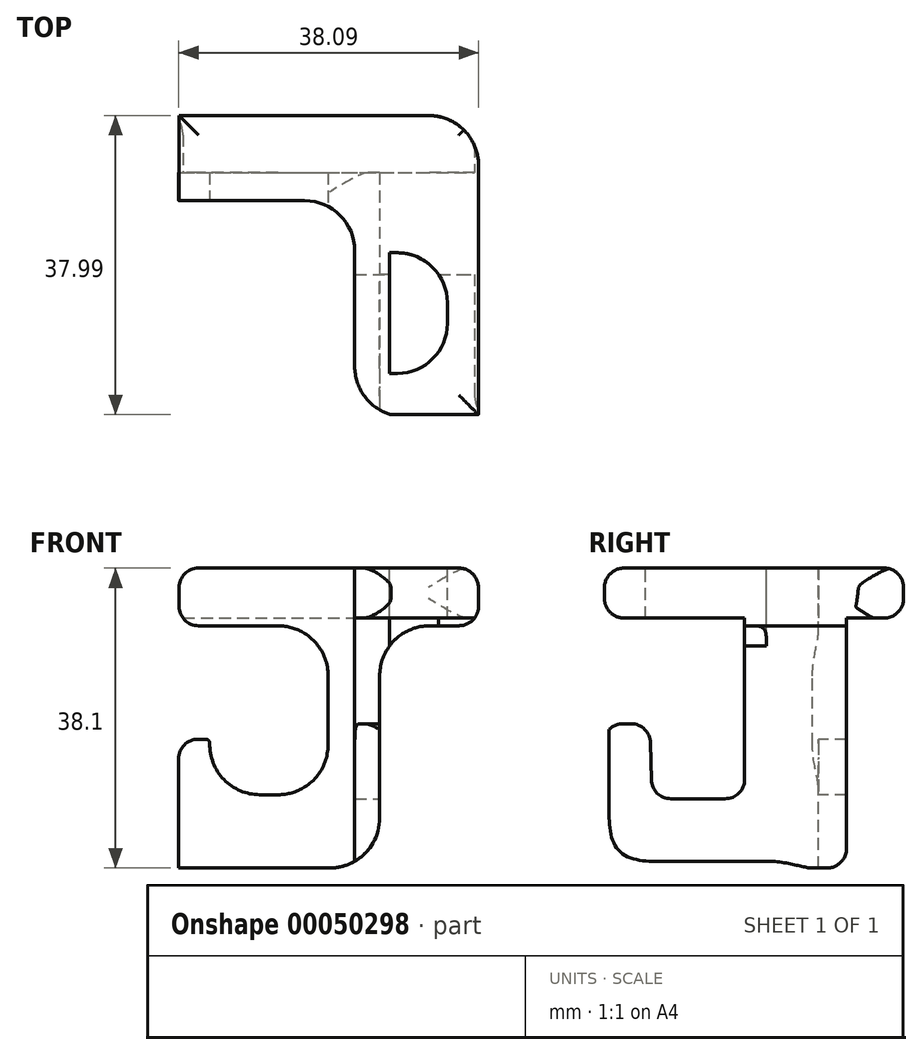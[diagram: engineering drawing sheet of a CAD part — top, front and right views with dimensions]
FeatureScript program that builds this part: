
annotation { "Feature Type Name" : "Feature", "Feature Type Description" : "" }
export const myFeature = defineFeature(function(context is Context, id is Id, definition is map)
    precondition{}
    {
        {
            var Q0;
            Q0=qCreatedBy(makeId("Front.planeOp"),FACE);
            var sketch = newSketch(context, id + "F0", { "sketchPlane" : qUnion([Q0])});
            skLineSegment(sketch, "E0", {"start": v(0, 0) * mm, "end": v(38.1, 0) * mm});
            skLineSegment(sketch, "E1", {"start": v(38.1, 0) * mm, "end": v(38.1, 38.1) * mm});
            skLineSegment(sketch, "E2", {"start": v(38.1, 38.1) * mm, "end": v(0, 38.1) * mm});
            skLineSegment(sketch, "E3", {"start": v(0, 38.1) * mm, "end": v(0, 0) * mm});
            skSolve(sketch);
        }
        {
            var Q0;
            Q0 = qSketchRegion(id + "F0", true);
            extrude(context, id + "F1", {"entities" : qUnion([Q0]), "depth" : 38.1 * mm});
        }
        {
            var Q0;
            Q0=qCreatedBy(makeId("Top.planeOp"),FACE);
            cPlane(context, id + "F2", {"entities" : qUnion([Q0]), "cplaneType" : CPlaneType.OFFSET, "offset" : 38.1 * mm, "width" : 152.4 * mm, "height" : 152.4 * mm});
        }
        {
            var Q0;
            Q0=qCreatedBy(makeId("Front.planeOp"),FACE);
            cPlane(context, id + "F3", {"entities" : qUnion([Q0]), "cplaneType" : CPlaneType.OFFSET, "offset" : 38.1 * mm, "width" : 152.4 * mm, "height" : 152.4 * mm});
        }
        {
            var Q0;
            Q0=qCreatedBy(makeId("Right.planeOp"),FACE);
            cPlane(context, id + "F4", {"entities" : qUnion([Q0]), "cplaneType" : CPlaneType.OFFSET, "offset" : 38.1 * mm, "width" : 152.4 * mm, "height" : 152.4 * mm});
        }
        {
            var Q0;
            Q0=qCreatedBy(id+"F3.planeOp",FACE);
            var sketch = newSketch(context, id + "F5", { "sketchPlane" : qUnion([Q0])});
            skLineSegment(sketch, "E4.bottom", {"start": v(0, 0) * mm, "end": v(38.1, 0) * mm});
            skLineSegment(sketch, "E4.top", {"start": v(0, 38.1) * mm, "end": v(38.1, 38.1) * mm});
            skLineSegment(sketch, "E4.left", {"start": v(0, 0) * mm, "end": v(0, 38.1) * mm});
            skLineSegment(sketch, "E4.right", {"start": v(38.1, 0) * mm, "end": v(38.1, 38.1) * mm});
            skPoint(sketch, "E5.startSnap0", {"position": v(19.05, 38.1) * mm});
            skLineSegment(sketch, "E6", {"start": v(2.51, 30.77) * mm, "end": v(12.05, 30.77) * mm});
            skLineSegment(sketch, "E7", {"start": v(12.05, 30.77) * mm, "end": v(12.63, 30.77) * mm});
            skLineSegment(sketch, "E8", {"start": v(18.98, 24.42) * mm, "end": v(18.98, 15.66) * mm});
            skLineSegment(sketch, "E9", {"start": v(12.63, 9.3) * mm, "end": v(11.17, 9.3) * mm});
            skLineSegment(sketch, "E10", {"start": v(4, 0) * mm, "end": v(19.18, 0) * mm});
            skLineSegment(sketch, "E11", {"start": v(25.53, 6.35) * mm, "end": v(25.53, 24.42) * mm});
            skLineSegment(sketch, "E12", {"start": v(31.88, 30.77) * mm, "end": v(35.62, 30.77) * mm});
            skLineSegment(sketch, "E13.left", {"start": v(0, 38.1) * mm, "end": v(0, 0) * mm});
            skLineSegment(sketch, "E13.right", {"start": v(38.1, 38.1) * mm, "end": v(38.1, 0) * mm});
            skLineSegment(sketch, "E14", {"start": v(3.45, 16.36) * mm, "end": v(2.47, 16.36) * mm});
            skLineSegment(sketch, "E15", {"start": v(0, 13.89) * mm, "end": v(0, 0) * mm});
            skLineSegment(sketch, "E16", {"start": v(11.17, 9.3) * mm, "end": v(10.3, 9.3) * mm});
            skPoint(sketch, "E17.visualSharp", {"position": v(4, 9.3) * mm});
            skArc(sketch, "E17.filletArc", {"start": v(3.96, 15.84) * mm, "mid": v(5.75, 11.23) * mm, "end": v(10.3, 9.3) * mm});
            skPoint(sketch, "E18.visualSharp", {"position": v(18.98, 9.3) * mm});
            skArc(sketch, "E18.filletArc", {"start": v(12.63, 9.3) * mm, "mid": v(17.12, 11.17) * mm, "end": v(18.98, 15.66) * mm});
            skPoint(sketch, "E19.visualSharp", {"position": v(25.53, 0) * mm});
            skArc(sketch, "E19.filletArc", {"start": v(19.18, 0) * mm, "mid": v(23.67, 1.86) * mm, "end": v(25.53, 6.35) * mm});
            skPoint(sketch, "E20.visualSharp", {"position": v(18.98, 30.77) * mm});
            skArc(sketch, "E20.filletArc", {"start": v(18.98, 24.42) * mm, "mid": v(17.12, 28.91) * mm, "end": v(12.63, 30.77) * mm});
            skPoint(sketch, "E21.visualSharp", {"position": v(25.53, 30.77) * mm});
            skArc(sketch, "E21.filletArc", {"start": v(31.88, 30.77) * mm, "mid": v(27.4, 28.91) * mm, "end": v(25.53, 24.42) * mm});
            skPoint(sketch, "E22.visualSharp", {"position": v(0, 16.36) * mm});
            skArc(sketch, "E22.filletArc", {"start": v(2.47, 16.36) * mm, "mid": v(0.72, 15.63) * mm, "end": v(0, 13.89) * mm});
            skLineSegment(sketch, "E23", {"start": v(0.04, 33.24) * mm, "end": v(0.04, 35.63) * mm});
            skLineSegment(sketch, "E24", {"start": v(2.51, 38.1) * mm, "end": v(35.6, 38.1) * mm});
            skLineSegment(sketch, "E25", {"start": v(38.07, 35.65) * mm, "end": v(38.1, 33.27) * mm});
            skPoint(sketch, "E26.visualSharp", {"position": v(0.04, 30.77) * mm});
            skArc(sketch, "E26.filletArc", {"start": v(0.04, 33.24) * mm, "mid": v(0.77, 31.5) * mm, "end": v(2.51, 30.77) * mm});
            skPoint(sketch, "E27.visualSharp", {"position": v(38.12, 30.77) * mm});
            skArc(sketch, "E27.filletArc", {"start": v(35.62, 30.77) * mm, "mid": v(37.38, 31.5) * mm, "end": v(38.1, 33.27) * mm});
            skPoint(sketch, "E28.visualSharp", {"position": v(38.04, 38.1) * mm});
            skArc(sketch, "E28.filletArc", {"start": v(38.07, 35.65) * mm, "mid": v(37.34, 37.39) * mm, "end": v(35.6, 38.1) * mm});
            skPoint(sketch, "E29.visualSharp", {"position": v(0.04, 38.1) * mm});
            skArc(sketch, "E29.filletArc", {"start": v(2.51, 38.1) * mm, "mid": v(0.77, 37.38) * mm, "end": v(0.04, 35.63) * mm});
            skPoint(sketch, "E30.visualSharp", {"position": v(4, 16.36) * mm});
            skArc(sketch, "E30.filletArc", {"start": v(3.96, 15.84) * mm, "mid": v(3.81, 16.2) * mm, "end": v(3.45, 16.36) * mm});
            skSolve(sketch);
        }
        {
            var Q0;
            Q0=qCreatedBy(id+"F4.planeOp",FACE);
            var sketch = newSketch(context, id + "F6", { "sketchPlane" : qUnion([Q0])});
            skLineSegment(sketch, "E31", {"start": v(-29.2, 31.75) * mm, "end": v(-20.19, 31.75) * mm});
            skLineSegment(sketch, "E32", {"start": v(-34.61, 18.32) * mm, "end": v(-35.63, 18.32) * mm});
            skLineSegment(sketch, "E33", {"start": v(-38.1, 15.85) * mm, "end": v(-38.1, 2.47) * mm});
            skLineSegment(sketch, "E34", {"start": v(-35.63, 0) * mm, "end": v(-9.72, 0) * mm});
            skLineSegment(sketch, "E35", {"start": v(-7.25, 2.47) * mm, "end": v(-7.25, 31.75) * mm});
            skLineSegment(sketch, "E36", {"start": v(-7.25, 31.75) * mm, "end": v(-2.47, 31.75) * mm});
            skLineSegment(sketch, "E37", {"start": v(0, 34.22) * mm, "end": v(0, 35.63) * mm});
            skLineSegment(sketch, "E38", {"start": v(-2.47, 38.1) * mm, "end": v(-35.52, 38.1) * mm});
            skLineSegment(sketch, "E39", {"start": v(-38, 35.63) * mm, "end": v(-38, 34.22) * mm});
            skLineSegment(sketch, "E40", {"start": v(-35.52, 31.75) * mm, "end": v(-29.2, 31.75) * mm});
            skLineSegment(sketch, "E41", {"start": v(-20.19, 31.75) * mm, "end": v(-20.19, 11.27) * mm});
            skLineSegment(sketch, "E42", {"start": v(-22.66, 8.8) * mm, "end": v(-29.57, 8.8) * mm});
            skLineSegment(sketch, "E43", {"start": v(-32.04, 11.21) * mm, "end": v(-32.14, 15.9) * mm});
            skPoint(sketch, "E44.visualSharp", {"position": v(-38, 31.75) * mm});
            skArc(sketch, "E44.filletArc", {"start": v(-38, 34.22) * mm, "mid": v(-37.27, 32.47) * mm, "end": v(-35.52, 31.75) * mm});
            skPoint(sketch, "E45.visualSharp", {"position": v(-38, 38.1) * mm});
            skArc(sketch, "E45.filletArc", {"start": v(-35.52, 38.1) * mm, "mid": v(-37.27, 37.38) * mm, "end": v(-38, 35.63) * mm});
            skPoint(sketch, "E46.visualSharp", {"position": v(0, 31.75) * mm});
            skArc(sketch, "E46.filletArc", {"start": v(-2.47, 31.75) * mm, "mid": v(-0.72, 32.47) * mm, "end": v(0, 34.22) * mm});
            skPoint(sketch, "E47.visualSharp", {"position": v(0, 38.1) * mm});
            skArc(sketch, "E47.filletArc", {"start": v(0, 35.63) * mm, "mid": v(-0.72, 37.38) * mm, "end": v(-2.47, 38.1) * mm});
            skPoint(sketch, "E48.visualSharp", {"position": v(-7.25, 0) * mm});
            skArc(sketch, "E48.filletArc", {"start": v(-9.72, 0) * mm, "mid": v(-7.97, 0.72) * mm, "end": v(-7.25, 2.47) * mm});
            skPoint(sketch, "E49.visualSharp", {"position": v(-20.19, 8.8) * mm});
            skArc(sketch, "E49.filletArc", {"start": v(-22.66, 8.8) * mm, "mid": v(-20.91, 9.52) * mm, "end": v(-20.19, 11.27) * mm});
            skPoint(sketch, "E50.visualSharp", {"position": v(-31.99, 8.8) * mm});
            skArc(sketch, "E50.filletArc", {"start": v(-32.04, 11.21) * mm, "mid": v(-31.3, 9.5) * mm, "end": v(-29.57, 8.8) * mm});
            skPoint(sketch, "E51.visualSharp", {"position": v(-32.2, 18.32) * mm});
            skArc(sketch, "E51.filletArc", {"start": v(-32.14, 15.9) * mm, "mid": v(-32.88, 17.61) * mm, "end": v(-34.61, 18.32) * mm});
            skPoint(sketch, "E52.visualSharp", {"position": v(-38.1, 18.32) * mm});
            skArc(sketch, "E52.filletArc", {"start": v(-35.63, 18.32) * mm, "mid": v(-37.38, 17.6) * mm, "end": v(-38.1, 15.85) * mm});
            skPoint(sketch, "E53.visualSharp", {"position": v(-38.1, 0) * mm});
            skArc(sketch, "E53.filletArc", {"start": v(-38.1, 2.47) * mm, "mid": v(-37.38, 0.72) * mm, "end": v(-35.63, 0) * mm});
            skLineSegment(sketch, "E54.bottom", {"start": v(-38.1, 0) * mm, "end": v(0, 0) * mm});
            skLineSegment(sketch, "E54.top", {"start": v(-38.1, 38.1) * mm, "end": v(0, 38.1) * mm});
            skLineSegment(sketch, "E54.left", {"start": v(-38.1, 0) * mm, "end": v(-38.1, 38.1) * mm});
            skLineSegment(sketch, "E54.right", {"start": v(0, 0) * mm, "end": v(0, 38.1) * mm});
            skSolve(sketch);
        }
        {
            var Q0;
            Q0=makeQuery(id+"F6.imprint","IMPRINT",FACE,{"disambiguationData":[TD([[makeQuery(id+"F6.imprint","IMPRINT",EDGE,{"derivedFrom":sQuery(id+"F6.wireOp",EDGE,"E31")}),-1.0]])]});
            var Q1;
            Q1=makeQuery(id+"F6.imprint","IMPRINT",FACE,{"disambiguationData":[TD([[makeQuery(id+"F6.imprint","IMPRINT",EDGE,{"derivedFrom":sQuery(id+"F6.wireOp",EDGE,"E35")}),-1.0]])]});
            var Q2;
            {var subQ0=sQuery(id+"F6.wireOp",EDGE,"E47.filletArc");Q2=makeQuery(id+"F6.imprint","IMPRINT",FACE,{"disambiguationData":[TD([[makeQuery(id+"F6.imprint","IMPRINT",EDGE,{"derivedFrom":subQ0}),-1.0]])]});}
            var Q3;
            {var subQ0=sQuery(id+"F6.wireOp",EDGE,"E53.filletArc");Q3=makeQuery(id+"F6.imprint","IMPRINT",FACE,{"disambiguationData":[TD([[makeQuery(id+"F6.imprint","IMPRINT",EDGE,{"derivedFrom":subQ0}),-1.0]])]});}
            extrude(context, id + "F7", {"entities" : qUnion([Q0, Q1, Q2, Q3]), "operationType" : NewBodyOperationType.REMOVE, "oppositeDirection" : true, "depth" : 38.1 * mm});
        }
        {
            var Q0;
            Q0=makeQuery(id+"F5.imprint","IMPRINT",FACE,{"disambiguationData":[TD([[makeQuery(id+"F5.imprint","IMPRINT",EDGE,{"derivedFrom":sQuery(id+"F5.wireOp",EDGE,"E6")}),-1.0]])]});
            var Q1;
            Q1=makeQuery(id+"F5.imprint","IMPRINT",FACE,{"disambiguationData":[TD([[makeQuery(id+"F5.imprint","IMPRINT",EDGE,{"derivedFrom":sQuery(id+"F5.wireOp",EDGE,"E11")}),-1.0]])]});
            extrude(context, id + "F8", {"entities" : qUnion([Q0, Q1]), "operationType" : NewBodyOperationType.REMOVE, "oppositeDirection" : true, "depth" : 38.1 * mm});
        }
        {
            var Q0;
            Q0=qCreatedBy(id+"F2.planeOp",FACE);
            var sketch = newSketch(context, id + "F9", { "sketchPlane" : qUnion([Q0])});
            skLineSegment(sketch, "E55", {"start": v(0, -10.83) * mm, "end": v(16.01, -10.83) * mm});
            skLineSegment(sketch, "E56", {"start": v(38.1, -38.24) * mm, "end": v(38.1, -6.35) * mm});
            skLineSegment(sketch, "E57", {"start": v(31.75, 0) * mm, "end": v(0, 0) * mm});
            skLineSegment(sketch, "E58", {"start": v(0, 0) * mm, "end": v(0, -10.83) * mm});
            skLineSegment(sketch, "E59", {"start": v(22.36, -17.18) * mm, "end": v(22.36, -31.7) * mm});
            skPoint(sketch, "E60.visualSharp", {"position": v(22.36, -10.83) * mm});
            skArc(sketch, "E60.filletArc", {"start": v(22.36, -17.18) * mm, "mid": v(20.5, -12.7) * mm, "end": v(16.01, -10.83) * mm});
            skPoint(sketch, "E61.visualSharp", {"position": v(22.36, -49.51) * mm});
            skPoint(sketch, "E62.visualSharp", {"position": v(38.1, 0) * mm});
            skArc(sketch, "E62.filletArc", {"start": v(38.1, -6.35) * mm, "mid": v(36.24, -1.86) * mm, "end": v(31.75, 0) * mm});
            skLineSegment(sketch, "E63", {"start": v(26.79, -17.44) * mm, "end": v(26.79, -32.76) * mm});
            skLineSegment(sketch, "E64", {"start": v(26.79, -32.76) * mm, "end": v(27.79, -32.76) * mm});
            skLineSegment(sketch, "E65", {"start": v(34.14, -26.4) * mm, "end": v(34.14, -23.79) * mm});
            skLineSegment(sketch, "E66", {"start": v(27.79, -17.44) * mm, "end": v(26.79, -17.44) * mm});
            skPoint(sketch, "E67.visualSharp", {"position": v(34.14, -17.44) * mm});
            skArc(sketch, "E67.filletArc", {"start": v(34.14, -23.79) * mm, "mid": v(32.28, -19.3) * mm, "end": v(27.79, -17.44) * mm});
            skPoint(sketch, "E68.visualSharp", {"position": v(34.14, -32.76) * mm});
            skArc(sketch, "E68.filletArc", {"start": v(27.79, -32.76) * mm, "mid": v(32.28, -30.9) * mm, "end": v(34.14, -26.4) * mm});
            skLineSegment(sketch, "E69", {"start": v(31.75, 0) * mm, "end": v(38.1, 0) * mm});
            skLineSegment(sketch, "E70", {"start": v(38.1, -6.35) * mm, "end": v(38.1, 0) * mm});
            skLineSegment(sketch, "E71", {"start": v(0, 0) * mm, "end": v(0, -38.3) * mm});
            skLineSegment(sketch, "E72", {"start": v(0, -38.3) * mm, "end": v(0.83, -38.24) * mm});
            skLineSegment(sketch, "E73.bottom", {"start": v(38.1, 0) * mm, "end": v(0, 0) * mm});
            skLineSegment(sketch, "E73.top", {"start": v(38.1, 0) * mm, "end": v(0, 0) * mm});
            skLineSegment(sketch, "E73.left", {"start": v(38.1, 0) * mm, "end": v(38.1, 0) * mm});
            skLineSegment(sketch, "E73.right", {"start": v(0, 0) * mm, "end": v(0, 0) * mm});
            skLineSegment(sketch, "E74.bottom", {"start": v(0, -38.3) * mm, "end": v(38.1, -38.3) * mm});
            skLineSegment(sketch, "E74.top", {"start": v(0, -38.24) * mm, "end": v(38.1, -38.24) * mm});
            skLineSegment(sketch, "E74.left", {"start": v(0, -38.3) * mm, "end": v(0, -38.24) * mm});
            skLineSegment(sketch, "E74.right", {"start": v(38.1, -38.3) * mm, "end": v(38.1, -38.24) * mm});
            skLineSegment(sketch, "E75.top", {"start": v(38.1, -38.24) * mm, "end": v(0, -38.24) * mm});
            skLineSegment(sketch, "E75.left", {"start": v(38.1, 0) * mm, "end": v(38.1, -38.24) * mm});
            skLineSegment(sketch, "E75.right", {"start": v(0, 0) * mm, "end": v(0, -38.24) * mm});
            skLineSegment(sketch, "E76", {"start": v(22.36, -31.7) * mm, "end": v(22.36, -31.89) * mm});
            skLineSegment(sketch, "E77", {"start": v(28.71, -38.24) * mm, "end": v(38.1, -38.24) * mm});
            skPoint(sketch, "E78.visualSharp", {"position": v(22.36, -38.24) * mm});
            skArc(sketch, "E78.filletArc", {"start": v(22.36, -31.89) * mm, "mid": v(24.22, -36.38) * mm, "end": v(28.71, -38.24) * mm});
            skSolve(sketch);
        }
        {
            var Q0;
            Q0=makeQuery(id+"F9.imprint","IMPRINT",FACE,{"disambiguationData":[TD([[makeQuery(id+"F9.imprint","IMPRINT",EDGE,{"derivedFrom":sQuery(id+"F9.wireOp",EDGE,"E63")}),1.0]])]});
            var Q1;
            Q1=makeQuery(id+"F9.imprint","IMPRINT",FACE,{"disambiguationData":[TD([[makeQuery(id+"F9.imprint","IMPRINT",EDGE,{"derivedFrom":sQuery(id+"F9.wireOp",EDGE,"E62.filletArc")}),-1.0]])]});
            var Q2;
            Q2=makeQuery(id+"F9.imprint","IMPRINT",FACE,{"disambiguationData":[TD([[makeQuery(id+"F9.imprint","IMPRINT",EDGE,{"derivedFrom":sQuery(id+"F9.wireOp",EDGE,"E55")}),-1.0]])]});
            extrude(context, id + "F10", {"entities" : qUnion([Q0, Q1, Q2]), "operationType" : NewBodyOperationType.REMOVE, "oppositeDirection" : true, "depth" : 38.1 * mm});
        }
    });
